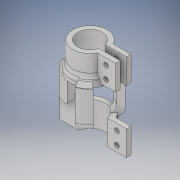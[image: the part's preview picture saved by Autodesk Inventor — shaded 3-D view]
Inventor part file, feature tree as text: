
AUTODESK INVENTOR PART (.ipt)
format: ipt  version: 2018 (Build 220112000, 112)  size: 363,520 bytes
history: native  units: in
note: dims shown in document units (in); Inventor stores cm internally (conversion verified against a paired STEP export)
features: fillet x6, extrude x5, sketch x5, projected_geometry x1
ambient origin geometry x8: Origin, YZ Plane, XZ Plane, XY Plane, X Axis, Y Axis, Z Axis, Center Point
bodies: Solid1 (feature_tree)
feature tree (17):
  extrude  "Extrusion1"  Depth=0.1875in
  extrude  "Extrusion2"  Depth=0.1875in
  extrude  "Extrusion3"  Depth=0.25in
  extrude  "Extrusion4"  TaperAngle=30.0deg  [1 undecoded]
  fillet  "Fillet1"  [1 undecoded]
  fillet  "Fillet3"  [1 undecoded]
  fillet  "Fillet4"  Radius=0.6528in
  fillet  "Fillet5"  Radius=0.6528in
  fillet  "Fillet6"  Radius=1.5in
  fillet  "Fillet7"  Radius=0.1875in
  extrude  "Extrusion5"  Depth=0.125in
  sketch  "Sketch1"  dims[d18=1.19in d19=0.1875in]
  sketch  "Sketch2"  dims[d20=0.1875in d21=0.75in d23=0.1875in]
  sketch  "Sketch3"  dims[d24=1.0in d25=0.0in d26=0.25in]
  sketch  "Sketch4"  dims[d27=1.5in d28=30.0deg d29=30.0deg d30=30.0deg d31=0.6528in d32=0.6528in d33=1.5in d34=0.0in d35=0.1875in]
  projected_geometry  "Projected Loop1"
  sketch  "Sketch5"  dims[d36=0.1875in d37=0.5in d38=0.25in d39=1.0in d40=0.0in d41=0.25in d42=0.0in d43=0.25in d45=0.25in d46=0.25in d47=0.25in d48=0.25in d49=0.25in d50=0.375in d51=0.375in d52=0.25in d53=0.25in d54=0.25in d55=0.25in d56=0.375in d57=0.375in d58=0.1935in d59=0.75in d60=0.0in d61=0.7825in d62=0.125in]
note: 3 required parameter values undecoded (feature->parameter linkage not recoverable at this tier; creation-order binding heuristic only, values carry confidence <= 0.55)
